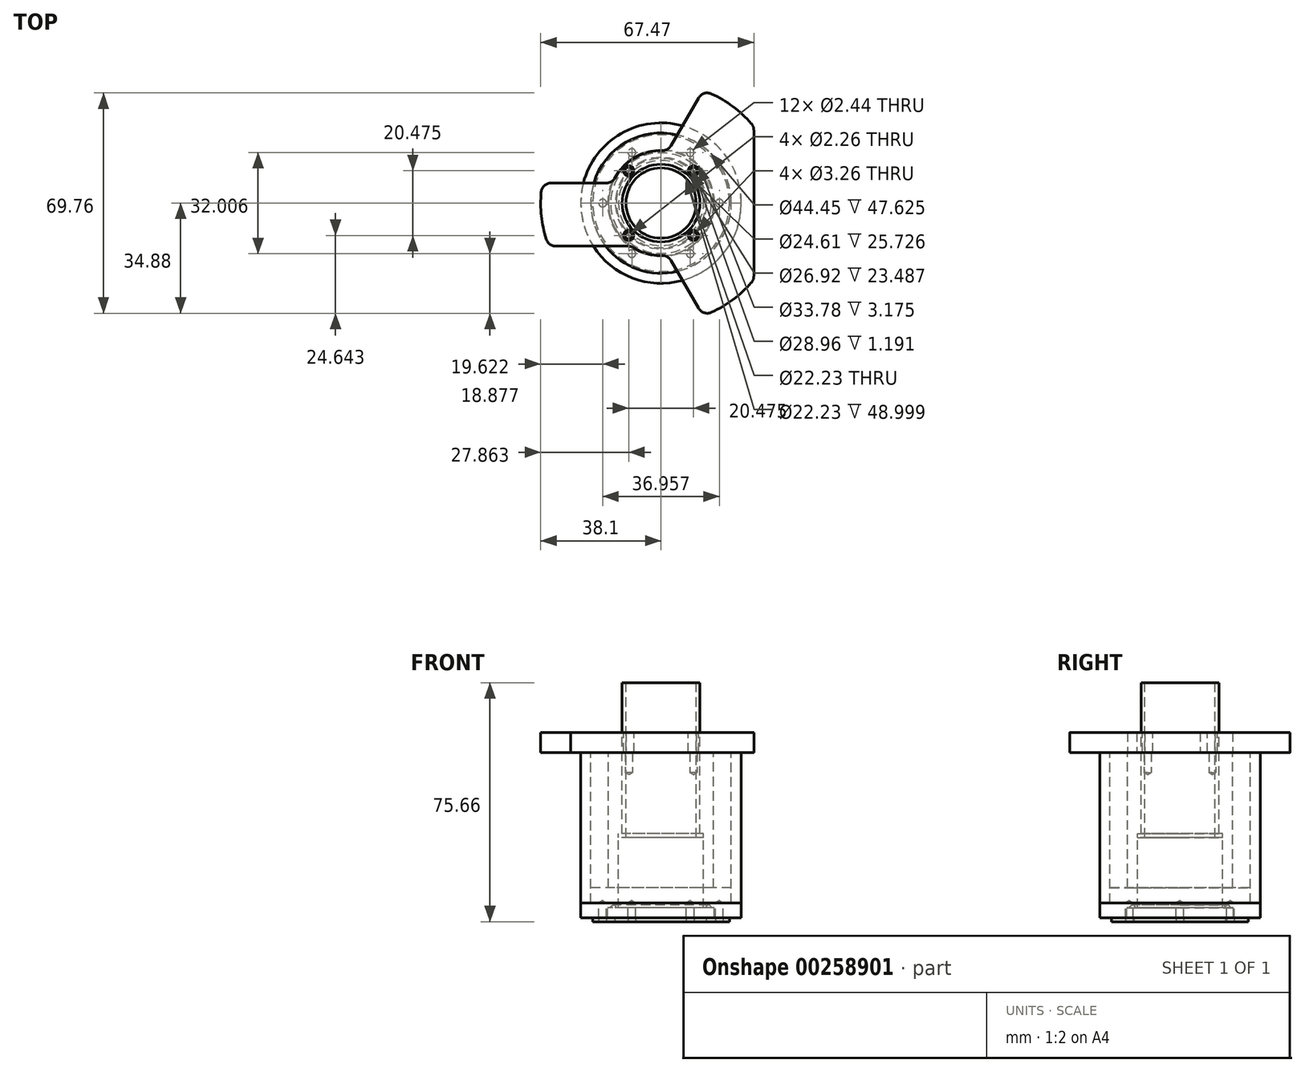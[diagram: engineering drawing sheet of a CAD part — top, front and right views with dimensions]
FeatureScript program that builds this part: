
annotation { "Feature Type Name" : "Feature", "Feature Type Description" : "" }
export const myFeature = defineFeature(function(context is Context, id is Id, definition is map)
    precondition{}
    {
        {
            var Q0;
            Q0=qCreatedBy(makeId("Top.planeOp"),FACE);
            var sketch = newSketch(context, id + "F0", { "sketchPlane" : qUnion([Q0])});
            skArc(sketch, "E0", {"start": v(28.57, 25.2) * mm, "mid": v(22.76, 30.55) * mm, "end": v(15.97, 34.6) * mm});
            skLineSegment(sketch, "E1", {"start": v(-34.78, 6.35) * mm, "end": v(-17.35, 6.35) * mm});
            skLineSegment(sketch, "E2", {"start": v(-34.78, -6.35) * mm, "end": v(-17.35, -6.35) * mm});
            skArc(sketch, "E3", {"start": v(-8.74, -14.13) * mm, "mid": v(-4.37, -16.03) * mm, "end": v(0.36, -16.61) * mm});
            skLineSegment(sketch, "E4.1.1", {"start": v(11.9, 33.3) * mm, "end": v(3.17, 18.2) * mm});
            skLineSegment(sketch, "E4.2.0", {"start": v(11.9, -33.3) * mm, "end": v(3.17, -18.2) * mm});
            skLineSegment(sketch, "E4.anchor1", {"start": v(0, 0) * mm, "end": v(-37.57, 6.35) * mm, "construction": true});
            skLineSegment(sketch, "E4.anchor2", {"start": v(0, 0) * mm, "end": v(13.28, -35.7) * mm, "construction": true});
            skArc(sketch, "E5.trimOffspring", {"start": v(0.36, 16.61) * mm, "mid": v(-8.3, 14.39) * mm, "end": v(-14.56, 8) * mm});
            skArc(sketch, "E6.trimOffspring", {"start": v(-37.94, 3.46) * mm, "mid": v(-37.88, -4.06) * mm, "end": v(-36.34, -11.43) * mm});
            skArc(sketch, "E7.trimOffspring", {"start": v(15.97, -34.6) * mm, "mid": v(22.76, -30.55) * mm, "end": v(28.57, -25.2) * mm});
            skLineSegment(sketch, "E8", {"start": v(29.37, 23.1) * mm, "end": v(29.37, -23.1) * mm});
            skCircle(sketch, "E9", {"center": v(0, 0) * mm, "radius": 11.11 * mm});
            skPoint(sketch, "E10.visualSharp", {"position": v(13.28, 35.7) * mm});
            skArc(sketch, "E10.filletArc", {"start": v(15.97, 34.6) * mm, "mid": v(13.68, 34.73) * mm, "end": v(11.9, 33.3) * mm});
            skPoint(sketch, "E11.visualSharp", {"position": v(29.37, 24.27) * mm});
            skArc(sketch, "E11.filletArc", {"start": v(29.37, 23.1) * mm, "mid": v(29.16, 24.22) * mm, "end": v(28.57, 25.2) * mm});
            skPoint(sketch, "E12.visualSharp", {"position": v(13.28, -35.7) * mm});
            skArc(sketch, "E12.filletArc", {"start": v(11.9, -33.3) * mm, "mid": v(13.68, -34.73) * mm, "end": v(15.97, -34.6) * mm});
            skPoint(sketch, "E13.visualSharp", {"position": v(29.37, -24.27) * mm});
            skArc(sketch, "E13.filletArc", {"start": v(28.57, -25.2) * mm, "mid": v(29.16, -24.22) * mm, "end": v(29.37, -23.1) * mm});
            skPoint(sketch, "E14.visualSharp", {"position": v(2.18, -16.47) * mm});
            skArc(sketch, "E14.filletArc", {"start": v(3.17, -18.2) * mm, "mid": v(1.98, -17.02) * mm, "end": v(0.36, -16.61) * mm});
            skPoint(sketch, "E15.visualSharp", {"position": v(2.18, 16.47) * mm});
            skArc(sketch, "E15.filletArc", {"start": v(0.36, 16.61) * mm, "mid": v(1.98, 17.02) * mm, "end": v(3.17, 18.2) * mm});
            skPoint(sketch, "E16.visualSharp", {"position": v(-15.35, 6.35) * mm});
            skArc(sketch, "E16.filletArc", {"start": v(-17.35, 6.35) * mm, "mid": v(-15.73, 6.8) * mm, "end": v(-14.56, 8) * mm});
            skPoint(sketch, "E17.visualSharp", {"position": v(-37.57, -6.35) * mm});
            skPoint(sketch, "E18.visualSharp", {"position": v(-37.57, 6.35) * mm});
            skArc(sketch, "E18.filletArc", {"start": v(-34.78, 6.35) * mm, "mid": v(-36.92, 5.52) * mm, "end": v(-37.94, 3.46) * mm});
            skLineSegment(sketch, "E19", {"start": v(-28.58, -13.66) * mm, "end": v(-10.4, -13.66) * mm});
            skPoint(sketch, "E20.visualSharp", {"position": v(-35.57, -13.66) * mm});
            skArc(sketch, "E20.filletArc", {"start": v(-36.34, -11.43) * mm, "mid": v(-35.2, -13.04) * mm, "end": v(-33.32, -13.66) * mm});
            skPoint(sketch, "E21.visualSharp", {"position": v(-9.46, -13.66) * mm});
            skArc(sketch, "E21.filletArc", {"start": v(-8.74, -14.13) * mm, "mid": v(-9.54, -13.78) * mm, "end": v(-10.4, -13.66) * mm});
            skLineSegment(sketch, "E22", {"start": v(28.58, -0.8) * mm, "end": v(28.58, -13.65) * mm});
            skLineSegment(sketch, "E23", {"start": v(15.88, -0.8) * mm, "end": v(15.88, -13.65) * mm});
            skLineSegment(sketch, "E24", {"start": v(-28.58, -0.8) * mm, "end": v(-15.88, -0.8) * mm});
            skLineSegment(sketch, "E25", {"start": v(-31.96, -13.65) * mm, "end": v(28.58, -13.65) * mm});
            skLineSegment(sketch, "E26.trimOffspring", {"start": v(-15.88, -0.8) * mm, "end": v(-15.88, -13.66) * mm});
            skLineSegment(sketch, "E27.trimOffspring", {"start": v(-28.58, -0.8) * mm, "end": v(-28.58, -13.66) * mm});
            skLineSegment(sketch, "E28.trimOffspring", {"start": v(15.88, -0.8) * mm, "end": v(28.58, -0.8) * mm});
            skLineSegment(sketch, "E29", {"start": v(-33.32, -13.66) * mm, "end": v(-31.96, -13.65) * mm});
            skLineSegment(sketch, "E30", {"start": v(-31.8, -10.02) * mm, "end": v(38.55, -10.02) * mm, "construction": true});
            skLineSegment(sketch, "E31.0", {"start": v(19.05, -0.8) * mm, "end": v(19.05, -13.65) * mm, "construction": true});
            skLineSegment(sketch, "E32.0", {"start": v(22.23, -0.8) * mm, "end": v(22.23, -13.65) * mm, "construction": true});
            skLineSegment(sketch, "E33.0", {"start": v(25.4, -0.8) * mm, "end": v(25.4, -13.65) * mm, "construction": true});
            skLineSegment(sketch, "E34.0", {"start": v(-19.05, -0.8) * mm, "end": v(-19.05, -13.66) * mm, "construction": true});
            skLineSegment(sketch, "E35.0", {"start": v(-22.23, -0.8) * mm, "end": v(-22.23, -13.66) * mm, "construction": true});
            skLineSegment(sketch, "E36.0", {"start": v(-25.4, -0.8) * mm, "end": v(-25.4, -13.66) * mm, "construction": true});
            skPoint(sketch, "E37", {"position": v(-25.4, -10.02) * mm});
            skPoint(sketch, "E38", {"position": v(-22.23, -10.02) * mm});
            skPoint(sketch, "E39", {"position": v(-19.05, -10.02) * mm});
            skPoint(sketch, "E40", {"position": v(15.88, -10.02) * mm});
            skPoint(sketch, "E41", {"position": v(19.05, -10.02) * mm});
            skPoint(sketch, "E42", {"position": v(22.23, -10.02) * mm});
            skPoint(sketch, "E43", {"position": v(25.4, -10.02) * mm});
            skSolve(sketch);
        }
        {
            var Q0;
            Q0=qSketchRegion(id+"F0",true);
            var Q1;
            {var subQ0=sQuery(id+"F0.wireOp",EDGE,"E22");Q1=makeQuery(id+"F0.imprint","IMPRINT",FACE,{"disambiguationData":[TD([[makeQuery(id+"F0.imprint","IMPRINT",EDGE,{"derivedFrom":subQ0}),-1.0]])]});}
            var Q2;
            Q2=makeQuery(id+"F0.imprint","IMPRINT",FACE,{"disambiguationData":[TD([[makeQuery(id+"F0.imprint","IMPRINT",EDGE,{"derivedFrom":sQuery(id+"F0.wireOp",EDGE,"5y2cDOX6-I3hJ-2pzI-yn7h-0IwxPdSi93P8")}),1.0]])]});
            var Q3;
            Q3=makeQuery(id+"F0.imprint","IMPRINT",FACE,{"disambiguationData":[TD([[makeQuery(id+"F0.imprint","IMPRINT",EDGE,{"derivedFrom":sQuery(id+"F0.wireOp",EDGE,"8gSkHoJA-c5vB-P1cI-9TfN-WfyGOhtXg48J")}),1.0]])]});
            var Q4;
            Q4=makeQuery(id+"F0.imprint","IMPRINT",FACE,{"disambiguationData":[TD([[makeQuery(id+"F0.imprint","IMPRINT",EDGE,{"derivedFrom":sQuery(id+"F0.wireOp",EDGE,"kiPsqy8w-5rV6-b9Iq-vhN1-elSIojTKA4aI")}),1.0]])]});
            var Q5;
            Q5=makeQuery(id+"F0.imprint","IMPRINT",FACE,{"disambiguationData":[TD([[makeQuery(id+"F0.imprint","IMPRINT",EDGE,{"derivedFrom":sQuery(id+"F0.wireOp",EDGE,"Hmd07uXR-aoQI-ZmvP-8Oo3-XdQevR7kfnbV")}),1.0]])]});
            extrude(context, id + "F1", {"entities" : qUnion([Q0, Q1, Q2, Q3, Q4, Q5]), "depth" : 6.35 * mm});
        }
        {
            var Q0;
            Q0=qCreatedBy(makeId("Front.planeOp"),FACE);
            var sketch = newSketch(context, id + "F2", { "sketchPlane" : qUnion([Q0])});
            skLineSegment(sketch, "E44", {"start": v(54.6, 79.01) * mm, "end": v(-46, 79.01) * mm, "construction": true});
            skLineSegment(sketch, "E45", {"start": v(-22.23, 91.3) * mm, "end": v(-22.23, 73.79) * mm, "construction": true});
            skLineSegment(sketch, "E46", {"start": v(22.23, 90.94) * mm, "end": v(22.23, 73.96) * mm, "construction": true});
            skCircle(sketch, "E47", {"center": v(22.23, 79.01) * mm, "radius": 4.76 * mm});
            skCircle(sketch, "E48", {"center": v(-22.23, 79.01) * mm, "radius": 4.76 * mm});
            skSolve(sketch);
        }
        {
            var Q0;
            Q0=qCreatedBy(makeId("Right.planeOp"),FACE);
            var sketch = newSketch(context, id + "F3", { "sketchPlane" : qUnion([Q0])});
            skPoint(sketch, "E49.0", {"position": v(0, 79.01) * mm});
            skLineSegment(sketch, "E50", {"start": v(0, 79.01) * mm, "end": v(53.17, 79.01) * mm, "construction": true});
            skLineSegment(sketch, "E51", {"start": v(11.11, -26.92) * mm, "end": v(13.46, -26.92) * mm});
            skLineSegment(sketch, "E52", {"start": v(0, 22.08) * mm, "end": v(11.11, 22.08) * mm});
            skLineSegment(sketch, "E53", {"start": v(11.11, 22.08) * mm, "end": v(11.11, -26.92) * mm});
            skLineSegment(sketch, "E54", {"start": v(0, -106.36) * mm, "end": v(13.46, -106.36) * mm});
            skLineSegment(sketch, "E55", {"start": v(13.46, -26.92) * mm, "end": v(13.46, -106.36) * mm});
            skLineSegment(sketch, "E56", {"start": v(0, 79.01) * mm, "end": v(0, -128.17) * mm, "construction": true});
            skLineSegment(sketch, "E57", {"start": v(-18.6, -52.39) * mm, "end": v(24.86, -52.39) * mm});
            skSolve(sketch);
        }
        {
            var Q0;
            Q0=qCreatedBy(makeId("Right.planeOp"),FACE);
            var sketch = newSketch(context, id + "F4", { "sketchPlane" : qUnion([Q0])});
            skLineSegment(sketch, "E58.0", {"start": v(0, -106.36) * mm, "end": v(13.46, -106.36) * mm});
            skLineSegment(sketch, "E59.0", {"start": v(13.46, -49.21) * mm, "end": v(13.46, -106.36) * mm});
            skLineSegment(sketch, "E60.0", {"start": v(-18.6, -52.39) * mm, "end": v(0, -52.39) * mm});
            skLineSegment(sketch, "E61.0", {"start": v(0, 79.01) * mm, "end": v(0, -128.17) * mm});
            skLineSegment(sketch, "E62.0", {"start": v(0, -106.62) * mm, "end": v(13.72, -106.62) * mm});
            skLineSegment(sketch, "E63.0", {"start": v(13.72, -52.39) * mm, "end": v(13.72, -106.62) * mm});
            skLineSegment(sketch, "E64", {"start": v(16.9, -49.21) * mm, "end": v(16.9, -52.39) * mm});
            skLineSegment(sketch, "E65", {"start": v(0, -49.21) * mm, "end": v(16.9, -49.21) * mm});
            skPoint(sketch, "E66.orphan", {"position": v(24.86, -52.39) * mm});
            skLineSegment(sketch, "E67.trimOffspring", {"start": v(13.72, -52.39) * mm, "end": v(16.9, -52.39) * mm});
            skPoint(sketch, "E68.orphan", {"position": v(13.46, -26.92) * mm});
            skSolve(sketch);
        }
        {
            var Q0;
            Q0=qCreatedBy(makeId("Right.planeOp"),FACE);
            var sketch = newSketch(context, id + "F5", { "sketchPlane" : qUnion([Q0])});
            skLineSegment(sketch, "E69.0", {"start": v(11.11, 22.08) * mm, "end": v(11.11, -26.92) * mm});
            skLineSegment(sketch, "E70.0", {"start": v(0, 22.08) * mm, "end": v(11.11, 22.08) * mm, "construction": true});
            skLineSegment(sketch, "E71.0", {"start": v(11.11, -26.92) * mm, "end": v(13.46, -26.92) * mm});
            skLineSegment(sketch, "E72.0", {"start": v(12.3, 22.08) * mm, "end": v(12.3, -25.73) * mm});
            skLineSegment(sketch, "E73.0", {"start": v(12.3, -25.73) * mm, "end": v(13.46, -25.73) * mm});
            skLineSegment(sketch, "E74", {"start": v(13.46, -25.73) * mm, "end": v(13.46, -26.92) * mm});
            skLineSegment(sketch, "E75", {"start": v(11.11, 22.08) * mm, "end": v(12.3, 22.08) * mm});
            skSolve(sketch);
        }
        {
            var Q0;
            Q0=makeQuery(id+"F5.imprint","IMPRINT",FACE,{"disambiguationData":[TD([[makeQuery(id+"F5.imprint","IMPRINT",EDGE,{"derivedFrom":sQuery(id+"F5.wireOp",EDGE,"E69.0")}),1.0]])]});
            var Q1;
            Q1=sQuery(id+"F3.wireOp",EDGE,"E56");
            revolve(context, id + "F6", {"entities" : qUnion([Q0]), "axis" : qUnion([Q1]), "revolveType" : RevolveType.FULL});
        }
        {
            var Q0;
            Q0=qCreatedBy(makeId("Right.planeOp"),FACE);
            var sketch = newSketch(context, id + "F7", { "sketchPlane" : qUnion([Q0])});
            skLineSegment(sketch, "E76.0", {"start": v(13.46, -26.92) * mm, "end": v(13.46, -106.36) * mm});
            skLineSegment(sketch, "E77.0", {"start": v(13.46, -25.73) * mm, "end": v(13.46, -26.92) * mm});
            skLineSegment(sketch, "E77.1", {"start": v(12.3, -25.73) * mm, "end": v(13.46, -25.73) * mm});
            skLineSegment(sketch, "E77.2", {"start": v(12.3, 22.08) * mm, "end": v(12.3, -25.73) * mm});
            skLineSegment(sketch, "E78.0", {"start": v(16.9, -49.21) * mm, "end": v(16.9, -52.39) * mm});
            skLineSegment(sketch, "E78.1", {"start": v(0, -49.21) * mm, "end": v(14.15, -49.21) * mm});
            skLineSegment(sketch, "E78.2", {"start": v(13.72, -52.39) * mm, "end": v(16.9, -52.39) * mm});
            skLineSegment(sketch, "E79", {"start": v(16.9, -52.39) * mm, "end": v(25.4, -52.39) * mm});
            skLineSegment(sketch, "E80", {"start": v(22.23, -47.63) * mm, "end": v(22.23, -42.86) * mm});
            skLineSegment(sketch, "E81", {"start": v(0, 0) * mm, "end": v(0, -49.21) * mm, "construction": true});
            skLineSegment(sketch, "E82", {"start": v(16.64, -42.86) * mm, "end": v(16.64, 0) * mm});
            skLineSegment(sketch, "E83.trimOffspring", {"start": v(16.64, -42.86) * mm, "end": v(22.23, -42.86) * mm});
            skLineSegment(sketch, "E84", {"start": v(12.3, 0) * mm, "end": v(16.64, 0) * mm});
            skLineSegment(sketch, "E85.0", {"start": v(25.4, -52.39) * mm, "end": v(25.4, -47.63) * mm});
            skLineSegment(sketch, "E86", {"start": v(22.23, -47.63) * mm, "end": v(25.4, -47.63) * mm});
            skArc(sketch, "E87", {"start": v(15.93, -49.21) * mm, "mid": v(15.04, -48.32) * mm, "end": v(14.15, -49.21) * mm});
            skLineSegment(sketch, "E88.trimOffspring", {"start": v(15.93, -49.21) * mm, "end": v(16.9, -49.21) * mm});
            skSolve(sketch);
        }
        {
            var Q0;
            Q0=qSketchRegion(id+"F7",true);
            var Q1;
            Q1=sQuery(id+"F7.wireOp",EDGE,"E81");
            revolve(context, id + "F8", {"entities" : qUnion([Q0]), "axis" : qUnion([Q1]), "revolveType" : RevolveType.FULL});
        }
        {
            var Q0;
            Q0=qCreatedBy(makeId("Right.planeOp"),FACE);
            var sketch = newSketch(context, id + "F9", { "sketchPlane" : qUnion([Q0])});
            skLineSegment(sketch, "E89.0", {"start": v(22.23, -47.63) * mm, "end": v(22.23, -42.86) * mm});
            skLineSegment(sketch, "E90.0", {"start": v(22.23, -47.63) * mm, "end": v(25.4, -47.63) * mm});
            skLineSegment(sketch, "E91.0", {"start": v(25.4, -52.39) * mm, "end": v(25.4, -47.63) * mm});
            skLineSegment(sketch, "E92", {"start": v(25.4, -47.63) * mm, "end": v(25.4, 0) * mm});
            skLineSegment(sketch, "E93", {"start": v(25.4, 0) * mm, "end": v(22.22, 0) * mm});
            skLineSegment(sketch, "E94", {"start": v(22.22, 0) * mm, "end": v(22.23, -47.63) * mm});
            skSolve(sketch);
        }
        {
            var Q0;
            Q0=qSketchRegion(id+"F9",true);
            var Q1;
            Q1=sQuery(id+"F7.wireOp",EDGE,"E81");
            revolve(context, id + "F10", {"entities" : qUnion([Q0]), "axis" : qUnion([Q1]), "revolveType" : RevolveType.FULL});
        }
        {
            var Q0;
            Q0=makeQuery(id+"F8.opRevolve","SWEPT_FACE",FACE,{"disambiguationData":[OSD([sQuery(id+"F7.wireOp",EDGE,"E79")])]});
            var sketch = newSketch(context, id + "F11", { "sketchPlane" : qUnion([Q0])});
            skLineSegment(sketch, "E95", {"start": v(0, 0) * mm, "end": v(-23, 0) * mm, "construction": true});
            skPoint(sketch, "E96", {"position": v(-18.48, 0) * mm});
            skPoint(sketch, "E97.1.0", {"position": v(-9.24, -16) * mm});
            skPoint(sketch, "E97.2.0", {"position": v(9.24, -16) * mm});
            skPoint(sketch, "E97.3.0", {"position": v(18.48, 0) * mm});
            skPoint(sketch, "E97.4.0", {"position": v(9.24, 16) * mm});
            skPoint(sketch, "E97.5.0", {"position": v(-9.24, 16) * mm});
            skPoint(sketch, "E97.center", {"position": v(0, 0) * mm});
            skCircle(sketch, "E98", {"center": v(0, 0) * mm, "radius": 14.48 * mm});
            skCircle(sketch, "E99.0", {"center": v(0, 0) * mm, "radius": 13.72 * mm, "construction": true});
            skCircle(sketch, "E100.0", {"center": v(0, 0) * mm, "radius": 21.63 * mm});
            skSolve(sketch);
        }
        {
            var Q0;
            Q0=sQuery(id+"F11.wireOp",VERTEX,"E96");
            var Q1;
            Q1=sQuery(id+"F11.wireOp",VERTEX,"E97.4.0");
            var Q2;
            Q2=sQuery(id+"F11.wireOp",VERTEX,"E97.3.0");
            var Q3;
            Q3=sQuery(id+"F11.wireOp",VERTEX,"E97.2.0");
            var Q4;
            Q4=sQuery(id+"F11.wireOp",VERTEX,"E97.1.0");
            var Q5;
            Q5=sQuery(id+"F11.wireOp",VERTEX,"E97.5.0");
            var Q6;
            Q6=makeQuery(id+"F8.opRevolve","SWEPT_BODY",BODY,{"disambiguationData":[OSD([sQuery(id+"F7.wireOp",EDGE,"E76.0"),sQuery(id+"F7.wireOp",EDGE,"E77.0"),sQuery(id+"F7.wireOp",EDGE,"E77.1"),sQuery(id+"F7.wireOp",EDGE,"E77.2"),sQuery(id+"F7.wireOp",EDGE,"E78.0"),sQuery(id+"F7.wireOp",EDGE,"E78.1"),sQuery(id+"F7.wireOp",EDGE,"E79"),sQuery(id+"F7.wireOp",EDGE,"E80"),sQuery(id+"F7.wireOp",EDGE,"E82"),sQuery(id+"F7.wireOp",EDGE,"E83.trimOffspring"),sQuery(id+"F7.wireOp",EDGE,"E84"),sQuery(id+"F7.wireOp",EDGE,"E85.0"),sQuery(id+"F7.wireOp",EDGE,"E86")])]});
            hole(context, id + "F12", {"style" : HoleStyle.SIMPLE, "endStyle" : HoleEndStyle.BLIND, "standardTappedOrClearance" : lookupTablePath({ "standard" : "ANSI", "fit" : "Normal (ASME)", "size" : "#2", "type" : "Clearance" }), "standardBlindInLast" : lookupTablePath({ "fit" : "Free", "standard" : "ANSI", "size" : "#2", "type" : "Clearance" }), "holeDiameter" : 2.44 * mm, "holeDepth" : 4.76 * mm, "locations" : qUnion([Q0, Q1, Q2, Q3, Q4, Q5]), "scope" : qUnion([Q6]), "startStyle" : HoleStartStyle.SKETCH});
        }
        {
            var Q0;
            Q0=qSketchRegion(id+"F11",true);
            var Q1;
            Q1=makeQuery(id+"FItFmHzJRnK65mm_7.opRevolve","SWEPT_FACE",FACE,{"disambiguationData":[OSD([sQuery(id+"F4.wireOp",EDGE,"E67.trimOffspring")])]});
            extrude(context, id + "F13", {"entities" : qUnion([Q0, Q1]), "depth" : 1.2 * mm});
        }
        {
            var Q0;
            Q0=sQuery(id+"F11.wireOp",VERTEX,"E97.4.0");
            var Q1;
            Q1=sQuery(id+"F11.wireOp",VERTEX,"E97.3.0");
            var Q2;
            Q2=sQuery(id+"F11.wireOp",VERTEX,"E97.2.0");
            var Q3;
            Q3=sQuery(id+"F11.wireOp",VERTEX,"E97.1.0");
            var Q4;
            Q4=sQuery(id+"F11.wireOp",VERTEX,"E96");
            var Q5;
            Q5=sQuery(id+"F11.wireOp",VERTEX,"E97.5.0");
            var Q6;
            Q6=makeQuery(id+"F13.opExtrude","SWEPT_BODY",BODY,{"disambiguationData":[OSD([sQuery(id+"F11.wireOp",EDGE,"E98"),sQuery(id+"F11.wireOp",EDGE,"E100.0")])]});
            hole(context, id + "F14", {"style" : HoleStyle.SIMPLE, "endStyle" : HoleEndStyle.THROUGH, "oppositeDirection" : true, "standardTappedOrClearance" : lookupTablePath({ "standard" : "ANSI", "fit" : "Normal (ASME)", "size" : "#2", "type" : "Clearance" }), "standardBlindInLast" : lookupTablePath({ "fit" : "Free", "standard" : "ANSI", "size" : "#2", "type" : "Clearance" }), "holeDiameter" : 2.44 * mm, "locations" : qUnion([Q0, Q1, Q2, Q3, Q4, Q5]), "scope" : qUnion([Q6]), "isTappedThrough" : true, "startStyle" : HoleStartStyle.SKETCH});
        }
        {
            var Q0;
            Q0=makeQuery(id+"F8.opRevolve","SWEPT_FACE",FACE,{"disambiguationData":[OSD([sQuery(id+"F7.wireOp",EDGE,"E84")])]});
            var sketch = newSketch(context, id + "F15", { "sketchPlane" : qUnion([Q0])});
            skCircle(sketch, "E101.0", {"center": v(0, 0) * mm, "radius": 12.3 * mm, "construction": true});
            skCircle(sketch, "E102.0", {"center": v(0, 0) * mm, "radius": 16.64 * mm, "construction": true});
            skLineSegment(sketch, "E103", {"start": v(0, 0) * mm, "end": v(-19.96, 0) * mm, "construction": true});
            skLineSegment(sketch, "E104", {"start": v(0, 0) * mm, "end": v(-13.64, 13.64) * mm, "construction": true});
            skPoint(sketch, "E105", {"position": v(-10.24, 10.24) * mm});
            skPoint(sketch, "E106.1.0", {"position": v(-10.24, -10.24) * mm});
            skPoint(sketch, "E106.2.0", {"position": v(10.24, -10.24) * mm});
            skPoint(sketch, "E106.3.0", {"position": v(10.24, 10.24) * mm});
            skSolve(sketch);
        }
        {
            var Q0;
            Q0=sQuery(id+"F15.wireOp",VERTEX,"E105");
            var Q1;
            Q1=sQuery(id+"F15.wireOp",VERTEX,"E106.3.0");
            var Q2;
            Q2=sQuery(id+"F15.wireOp",VERTEX,"E106.2.0");
            var Q3;
            Q3=sQuery(id+"F15.wireOp",VERTEX,"E106.1.0");
            var Q4;
            Q4=makeQuery(id+"F8.opRevolve","SWEPT_BODY",BODY,{"disambiguationData":[OSD([sQuery(id+"F7.wireOp",EDGE,"E76.0"),sQuery(id+"F7.wireOp",EDGE,"E77.0"),sQuery(id+"F7.wireOp",EDGE,"E77.1"),sQuery(id+"F7.wireOp",EDGE,"E77.2"),sQuery(id+"F7.wireOp",EDGE,"E78.0"),sQuery(id+"F7.wireOp",EDGE,"E78.1"),sQuery(id+"F7.wireOp",EDGE,"E79"),sQuery(id+"F7.wireOp",EDGE,"E80"),sQuery(id+"F7.wireOp",EDGE,"E82"),sQuery(id+"F7.wireOp",EDGE,"E83.trimOffspring"),sQuery(id+"F7.wireOp",EDGE,"E84"),sQuery(id+"F7.wireOp",EDGE,"E85.0"),sQuery(id+"F7.wireOp",EDGE,"E86"),sQuery(id+"F7.wireOp",EDGE,"E87"),sQuery(id+"F7.wireOp",EDGE,"E88.trimOffspring")])]});
            hole(context, id + "F16", {"style" : HoleStyle.SIMPLE, "endStyle" : HoleEndStyle.BLIND, "standardTappedOrClearance" : lookupTablePath({ "standard" : "ANSI", "engagement" : "75%", "pitch" : "40 tpi", "size" : "#4", "type" : "Tapped" }), "standardBlindInLast" : lookupTablePath({ "standard" : "ANSI", "engagement" : "75%", "pitch" : "40 tpi", "size" : "#4", "type" : "Tapped" }), "holeDiameter" : 2.26 * mm, "holeDepth" : 6.35 * mm, "locations" : qUnion([Q0, Q1, Q2, Q3]), "scope" : qUnion([Q4]), "majorDiameter" : 2.84 * mm, "startStyle" : HoleStartStyle.SKETCH});
        }
        {
            var Q0;
            Q0=sQuery(id+"F15.wireOp",VERTEX,"E105");
            var Q1;
            Q1=sQuery(id+"F15.wireOp",VERTEX,"E106.3.0");
            var Q2;
            Q2=sQuery(id+"F15.wireOp",VERTEX,"E106.2.0");
            var Q3;
            Q3=sQuery(id+"F15.wireOp",VERTEX,"E106.1.0");
            var Q4;
            Q4=makeQuery(id+"F1.opExtrude","SWEPT_BODY",BODY,{"disambiguationData":[OSD([sQuery(id+"F0.wireOp",EDGE,"E0"),sQuery(id+"F0.wireOp",EDGE,"E1"),sQuery(id+"F0.wireOp",EDGE,"E3"),sQuery(id+"F0.wireOp",EDGE,"E4.1.1"),sQuery(id+"F0.wireOp",EDGE,"E4.2.0"),sQuery(id+"F0.wireOp",EDGE,"E5.trimOffspring"),sQuery(id+"F0.wireOp",EDGE,"E6.trimOffspring"),sQuery(id+"F0.wireOp",EDGE,"E7.trimOffspring"),sQuery(id+"F0.wireOp",EDGE,"E8"),sQuery(id+"F0.wireOp",EDGE,"E9"),sQuery(id+"F0.wireOp",EDGE,"E10.filletArc"),sQuery(id+"F0.wireOp",EDGE,"E11.filletArc"),sQuery(id+"F0.wireOp",EDGE,"E12.filletArc"),sQuery(id+"F0.wireOp",EDGE,"E13.filletArc"),sQuery(id+"F0.wireOp",EDGE,"E14.filletArc"),sQuery(id+"F0.wireOp",EDGE,"E15.filletArc"),sQuery(id+"F0.wireOp",EDGE,"E16.filletArc"),sQuery(id+"F0.wireOp",EDGE,"E18.filletArc"),sQuery(id+"F0.wireOp",EDGE,"E19"),sQuery(id+"F0.wireOp",EDGE,"E20.filletArc"),sQuery(id+"F0.wireOp",EDGE,"E21.filletArc"),sQuery(id+"F0.wireOp",EDGE,"E25"),sQuery(id+"F0.wireOp",EDGE,"E27.trimOffspring"),sQuery(id+"F0.wireOp",EDGE,"E29")])]});
            hole(context, id + "F17", {"style" : HoleStyle.SIMPLE, "endStyle" : HoleEndStyle.THROUGH, "oppositeDirection" : true, "standardTappedOrClearance" : lookupTablePath({ "standard" : "ANSI", "fit" : "Normal (ASME)", "size" : "#4", "type" : "Clearance" }), "standardBlindInLast" : lookupTablePath({ "fit" : "Free", "standard" : "ANSI", "size" : "#4", "type" : "Clearance" }), "holeDiameter" : 3.26 * mm, "locations" : qUnion([Q0, Q1, Q2, Q3]), "scope" : qUnion([Q4]), "isTappedThrough" : true, "startStyle" : HoleStartStyle.SKETCH});
        }
    });
